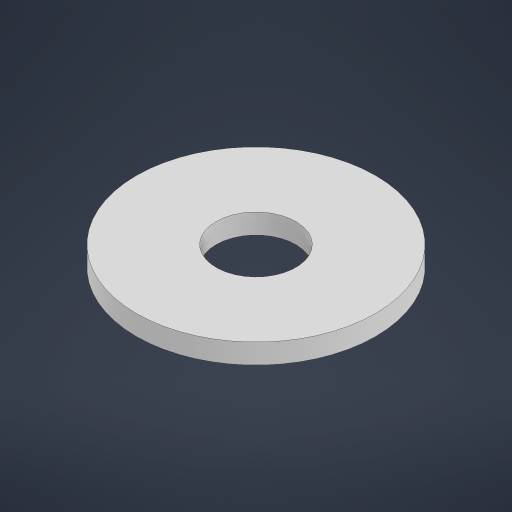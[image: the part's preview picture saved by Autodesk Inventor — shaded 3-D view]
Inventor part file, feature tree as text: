
AUTODESK INVENTOR PART (.ipt)
format: ipt  version: 2024 (Build 280153000, 153)  size: 162,304 bytes
history: native  units: in
note: dims shown in document units (in); Inventor stores cm internally (conversion verified against a paired STEP export)
features: extrude x1, sketch x1
ambient origin geometry x8: Origin, YZ Plane, XZ Plane, XY Plane, X Axis, Y Axis, Z Axis, Center Point
bodies: Solid1 (feature_tree)
feature tree (2):
  extrude  "Extrusion1"  Depth=0.0394in
  sketch  "Sketch1"  dims[d0=0.1575in d1=0.4724in d2=0.0394in d3=0.0in]
